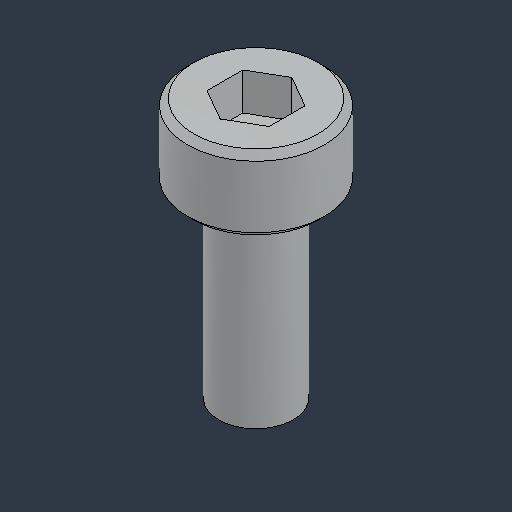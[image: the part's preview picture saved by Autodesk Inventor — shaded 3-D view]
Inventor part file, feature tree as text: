
AUTODESK INVENTOR PART (.ipt)
format: ipt  version: 2024.3 (Build 283343000, 343)  size: 102,912 bytes
history: native  units: in
note: dims shown in document units (in); Inventor stores cm internally (conversion verified against a paired STEP export)
features: chamfer x1
ambient origin geometry x8: Origin, YZ Plane, XZ Plane, XY Plane, X Axis, Y Axis, Z Axis, Center Point
bodies: Solid1 (feature_tree)
feature tree (1):
  chamfer  "Chamfer2"  [1 undecoded]
note: 1 required parameter value undecoded (feature->parameter linkage not recoverable at this tier; creation-order binding heuristic only, values carry confidence <= 0.55)
